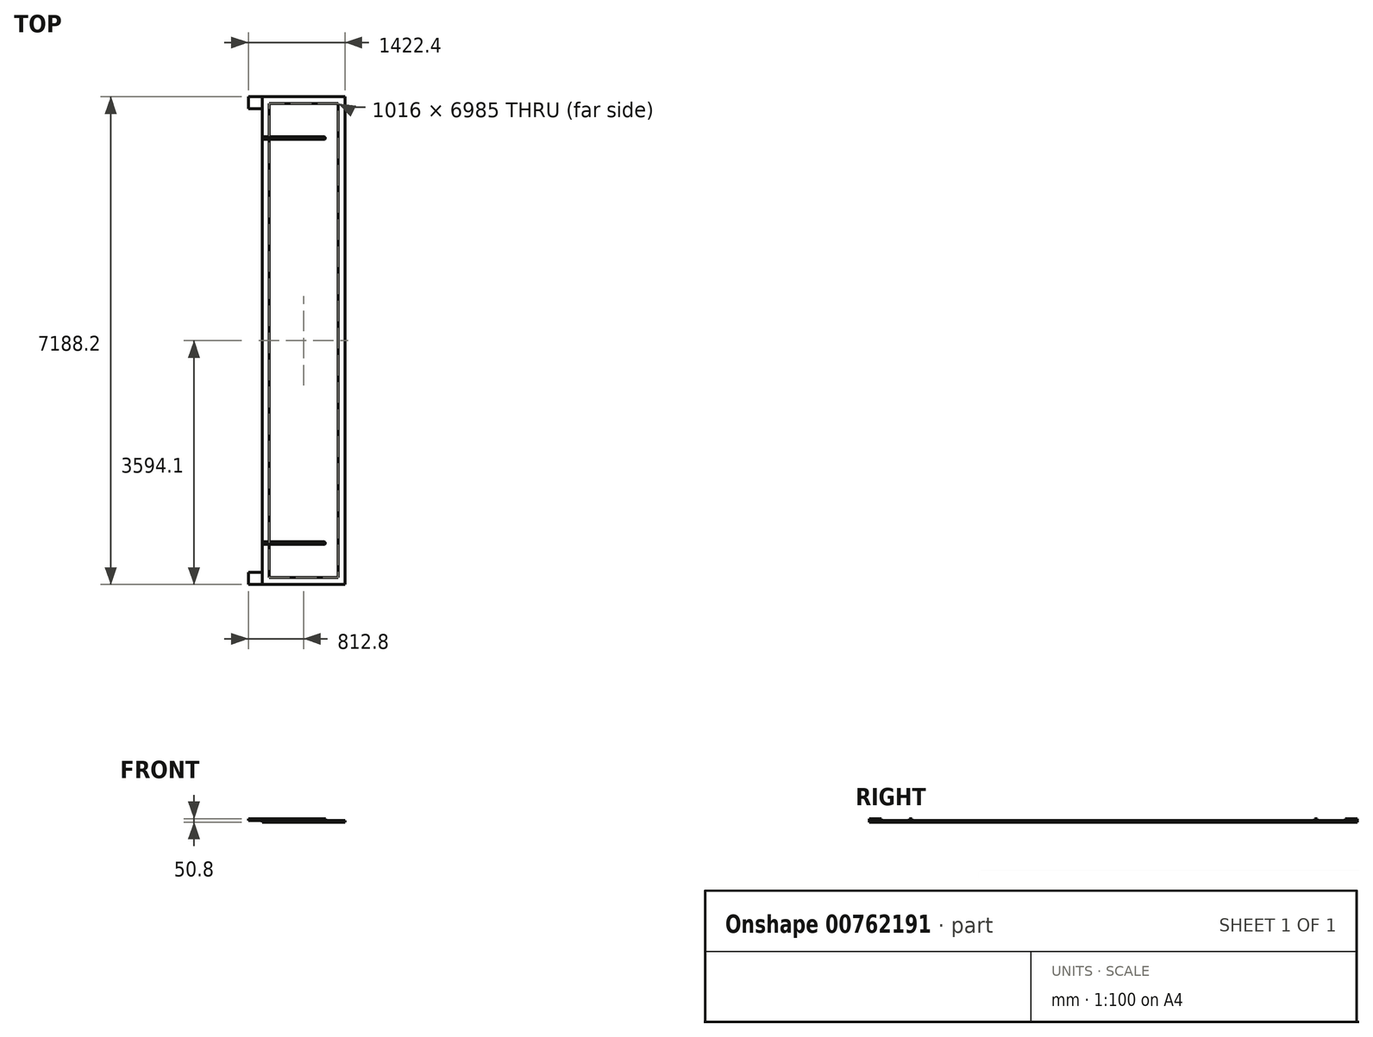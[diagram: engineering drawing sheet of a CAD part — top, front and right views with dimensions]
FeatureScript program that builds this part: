
annotation { "Feature Type Name" : "Feature", "Feature Type Description" : "" }
export const myFeature = defineFeature(function(context is Context, id is Id, definition is map)
    precondition{}
    {
        {
            var Q0;
            Q0=qCreatedBy(makeId("Top.planeOp"),FACE);
            var sketch = newSketch(context, id + "F0", { "sketchPlane" : qUnion([Q0])});
            skLineSegment(sketch, "E0.bottom", {"start": v(0, 0) * mm, "end": v(1219.2, 0) * mm});
            skLineSegment(sketch, "E0.top", {"start": v(0, -7188.2) * mm, "end": v(1219.2, -7188.2) * mm});
            skLineSegment(sketch, "E0.left", {"start": v(0, 0) * mm, "end": v(0, -7188.2) * mm});
            skLineSegment(sketch, "E0.right", {"start": v(1219.2, 0) * mm, "end": v(1219.2, -7188.2) * mm});
            skLineSegment(sketch, "E1.bottom", {"start": v(101.6, -101.6) * mm, "end": v(1117.6, -101.6) * mm});
            skLineSegment(sketch, "E1.top", {"start": v(101.6, -7086.6) * mm, "end": v(1117.6, -7086.6) * mm});
            skLineSegment(sketch, "E1.left", {"start": v(101.6, -101.6) * mm, "end": v(101.6, -7086.6) * mm});
            skLineSegment(sketch, "E1.right", {"start": v(1117.6, -101.6) * mm, "end": v(1117.6, -7086.6) * mm});
            skSolve(sketch);
        }
        {
            var Q0;
            Q0 = qSketchRegion(id + "F0", true);
            extrude(context, id + "F1", {"entities" : qUnion([Q0]), "depth" : 25.4 * mm, "offsetDistance" : 25.4 * mm});
        }
        {
            var Q0;
            Q0=makeQuery(id+"F1.opExtrude","CAP_FACE",FACE,{"disambiguationData":[OSD([sQuery(id+"F0.wireOp",EDGE,"E0.bottom"),sQuery(id+"F0.wireOp",EDGE,"E0.top"),sQuery(id+"F0.wireOp",EDGE,"E0.left"),sQuery(id+"F0.wireOp",EDGE,"E0.right"),sQuery(id+"F0.wireOp",EDGE,"E1.bottom"),sQuery(id+"F0.wireOp",EDGE,"E1.top"),sQuery(id+"F0.wireOp",EDGE,"E1.left"),sQuery(id+"F0.wireOp",EDGE,"E1.right")])],"isStart":false});
            var sketch = newSketch(context, id + "F2", { "sketchPlane" : qUnion([Q0])});
            skLineSegment(sketch, "E2.bottom", {"start": v(0, 0) * mm, "end": v(-203.2, 0) * mm});
            skLineSegment(sketch, "E2.top", {"start": v(0, -177.8) * mm, "end": v(-203.2, -177.8) * mm});
            skLineSegment(sketch, "E2.left", {"start": v(0, 0) * mm, "end": v(0, -177.8) * mm});
            skLineSegment(sketch, "E2.right", {"start": v(-203.2, 0) * mm, "end": v(-203.2, -177.8) * mm});
            skLineSegment(sketch, "E3.bottom", {"start": v(0, -7188.2) * mm, "end": v(-203.2, -7188.2) * mm});
            skLineSegment(sketch, "E3.top", {"start": v(0, -7010.4) * mm, "end": v(-203.2, -7010.4) * mm});
            skLineSegment(sketch, "E3.left", {"start": v(0, -7188.2) * mm, "end": v(0, -7010.4) * mm});
            skLineSegment(sketch, "E3.right", {"start": v(-203.2, -7188.2) * mm, "end": v(-203.2, -7010.4) * mm});
            skLineSegment(sketch, "E4.bottom", {"start": v(0, -590.55) * mm, "end": v(914.4, -590.55) * mm});
            skLineSegment(sketch, "E4.top", {"start": v(0, -628.65) * mm, "end": v(914.4, -628.65) * mm});
            skLineSegment(sketch, "E4.left", {"start": v(0, -590.55) * mm, "end": v(0, -628.65) * mm});
            skLineSegment(sketch, "E4.right", {"start": v(914.4, -590.55) * mm, "end": v(914.4, -628.65) * mm});
            skLineSegment(sketch, "E5.bottom", {"start": v(0, -6559.55) * mm, "end": v(914.4, -6559.55) * mm});
            skLineSegment(sketch, "E5.top", {"start": v(0, -6597.65) * mm, "end": v(914.4, -6597.65) * mm});
            skLineSegment(sketch, "E5.left", {"start": v(0, -6559.55) * mm, "end": v(0, -6597.65) * mm});
            skLineSegment(sketch, "E5.right", {"start": v(914.4, -6559.55) * mm, "end": v(914.4, -6597.65) * mm});
            skCircle(sketch, "E6", {"center": v(914.4, -6578.6) * mm, "radius": 19.05 * mm});
            skCircle(sketch, "E7", {"center": v(914.4, -609.6) * mm, "radius": 19.05 * mm});
            skSolve(sketch);
        }
        {
            var Q0;
            Q0 = qSketchRegion(id + "F2", true);
            extrude(context, id + "F3", {"entities" : qUnion([Q0]), "depth" : 25.4 * mm, "offsetDistance" : 25.4 * mm});
        }
    });
